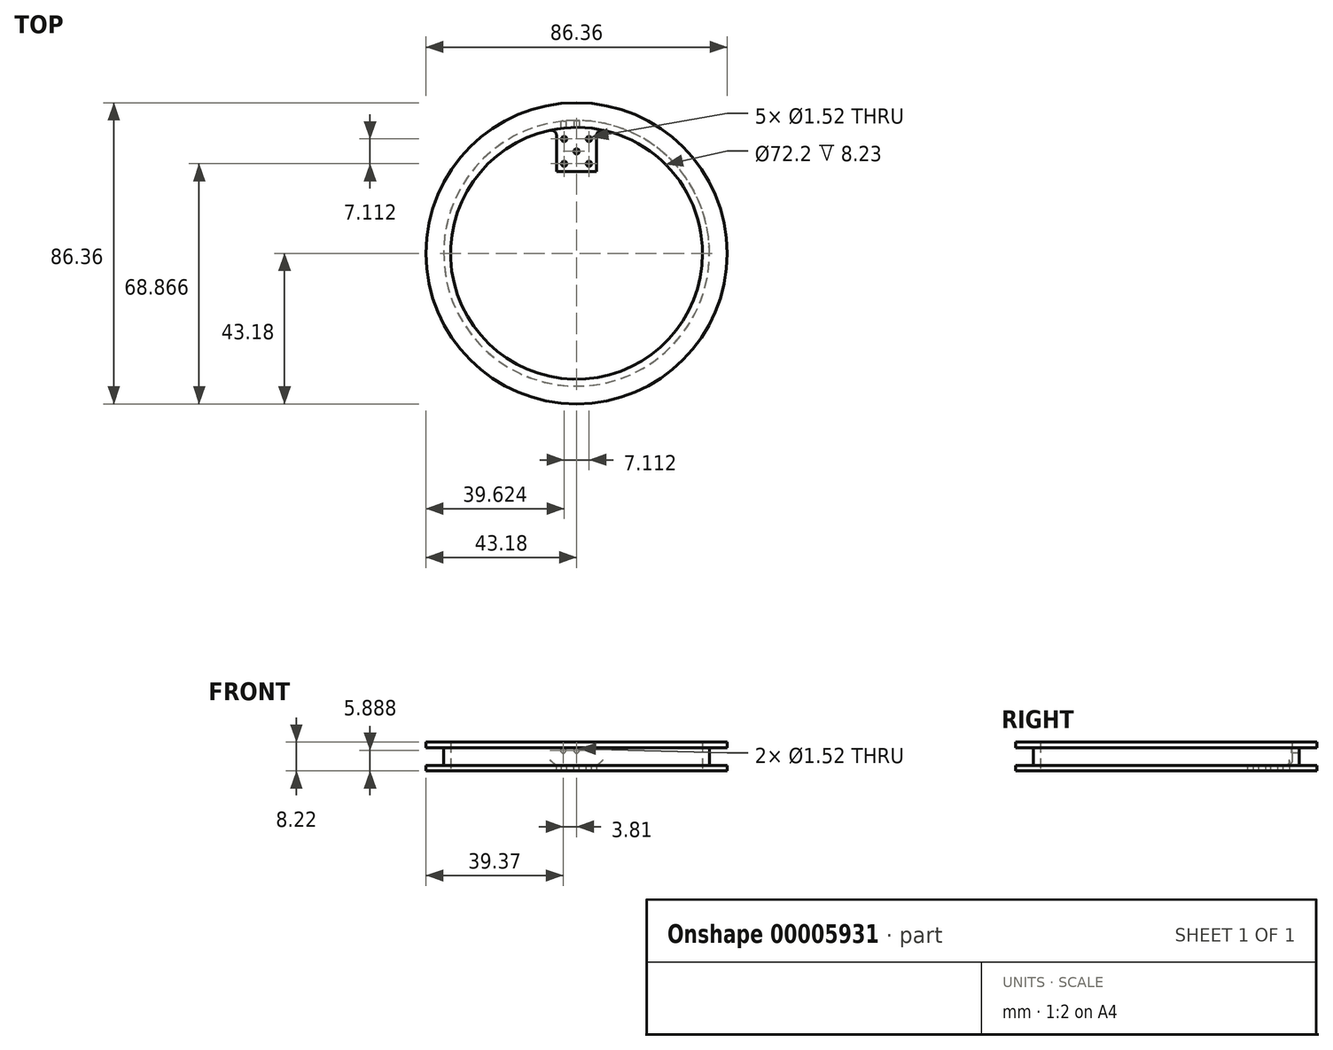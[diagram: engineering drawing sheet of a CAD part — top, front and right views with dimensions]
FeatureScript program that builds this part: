
annotation { "Feature Type Name" : "Feature", "Feature Type Description" : "" }
export const myFeature = defineFeature(function(context is Context, id is Id, definition is map)
    precondition{}
    {
        {
            var Q0;
            Q0=qCreatedBy(makeId("Top.planeOp"),FACE);
            var sketch = newSketch(context, id + "F0", { "sketchPlane" : qUnion([Q0])});
            skCircle(sketch, "E0", {"center": v(0, 0) * mm, "radius": 38.1 * mm});
            skCircle(sketch, "E1.0", {"center": v(0, 0) * mm, "radius": 36.1 * mm});
            skSolve(sketch);
        }
        {
            var Q0;
            Q0 = qSketchRegion(id + "F0", true);
            extrude(context, id + "F1", {"entities" : qUnion([Q0]), "depth" : 5.08 * mm});
        }
        {
            var Q0;
            Q0=qCreatedBy(makeId("Top.planeOp"),FACE);
            var sketch = newSketch(context, id + "F2", { "sketchPlane" : qUnion([Q0])});
            skCircle(sketch, "E2", {"center": v(0, 0) * mm, "radius": 43.18 * mm});
            skCircle(sketch, "E3", {"center": v(0, 0) * mm, "radius": 36.1 * mm});
            skSolve(sketch);
        }
        {
            var Q0;
            Q0 = qSketchRegion(id + "F2", true);
            extrude(context, id + "F3", {"entities" : qUnion([Q0]), "operationType" : NewBodyOperationType.ADD, "oppositeDirection" : true, "depth" : 1.57 * mm});
        }
        {
            var Q0;
            Q0=qCreatedBy(makeId("Top.planeOp"),FACE);
            var Q1;
            Q1=makeQuery(id+"F1.opExtrude","CAP_FACE",FACE,{"disambiguationData":[OSD([sQuery(id+"F0.wireOp",EDGE,"E0"),sQuery(id+"F0.wireOp",EDGE,"E1.0")])],"isStart":false});
            cPlane(context, id + "F4", {"entities" : qUnion([Q0, Q1]), "cplaneType" : CPlaneType.MID_PLANE, "offset" : 152.4 * mm, "width" : 152.4 * mm, "height" : 152.4 * mm});
        }
        {
            var Q0;
            Q0=makeQuery(id+"F1.opExtrude","SWEPT_BODY",BODY,{"disambiguationData":[OSD([sQuery(id+"F0.wireOp",EDGE,"E0"),sQuery(id+"F0.wireOp",EDGE,"E1.0")])]});
            var Q1;
            Q1=qCreatedBy(id+"F4.planeOp",FACE);
            mirror(context, id + "F5", {"entities" : qUnion([Q0]), "mirrorPlane" : qUnion([Q1])});
        }
        {
            var Q0;
            Q0=qCreatedBy(makeId("Top.planeOp"),FACE);
            var sketch = newSketch(context, id + "F6", { "sketchPlane" : qUnion([Q0])});
            skLineSegment(sketch, "E4.bottom", {"start": v(-5.72, 36.1) * mm, "end": v(5.72, 36.1) * mm});
            skLineSegment(sketch, "E4.top", {"start": v(-5.71, 23.4) * mm, "end": v(5.71, 23.4) * mm});
            skLineSegment(sketch, "E4.left", {"start": v(-5.72, 36.1) * mm, "end": v(-5.72, 23.4) * mm});
            skLineSegment(sketch, "E4.right", {"start": v(5.72, 36.1) * mm, "end": v(5.72, 23.4) * mm});
            skPoint(sketch, "E5", {"position": v(0, 36.1) * mm});
            skLineSegment(sketch, "E6.bottom", {"start": v(-3.56, 32.8) * mm, "end": v(3.56, 32.8) * mm, "construction": true});
            skLineSegment(sketch, "E6.top", {"start": v(-3.56, 25.69) * mm, "end": v(3.56, 25.69) * mm, "construction": true});
            skLineSegment(sketch, "E6.left", {"start": v(-3.56, 32.8) * mm, "end": v(-3.56, 25.69) * mm, "construction": true});
            skLineSegment(sketch, "E6.right", {"start": v(3.56, 32.8) * mm, "end": v(3.56, 25.69) * mm, "construction": true});
            skCircle(sketch, "E7", {"center": v(-3.56, 32.8) * mm, "radius": 0.76 * mm});
            skCircle(sketch, "E8", {"center": v(3.56, 32.8) * mm, "radius": 0.76 * mm});
            skCircle(sketch, "E9", {"center": v(3.56, 25.69) * mm, "radius": 0.76 * mm});
            skCircle(sketch, "E10", {"center": v(-3.56, 25.69) * mm, "radius": 0.76 * mm});
            skLineSegment(sketch, "E11", {"start": v(-3.56, 25.69) * mm, "end": v(3.56, 32.8) * mm, "construction": true});
            skCircle(sketch, "E12", {"center": v(0, 29.24) * mm, "radius": 0.76 * mm});
            skSolve(sketch);
        }
        {
            var Q0;
            Q0 = qSketchRegion(id + "F6", true);
            var Q1;
            Q1=makeQuery(id+"F3.opExtrude","CAP_FACE",FACE,{"disambiguationData":[OSD([sQuery(id+"F2.wireOp",EDGE,"E2"),sQuery(id+"F2.wireOp",EDGE,"E3")])],"isStart":false});
            extrude(context, id + "F7", {"entities" : qUnion([Q0]), "operationType" : NewBodyOperationType.ADD, "endBound" : BoundingType.UP_TO_SURFACE, "oppositeDirection" : true, "endBoundEntityFace" : qUnion([Q1]), "depth" : 25.4 * mm});
        }
        {
            var Q0;
            Q0=makeQuery(id+"F7.boolean.opBoolean","INTERSECT",EDGE,{"derivedFrom":[makeQuery(id+"F5.opPattern","COPY",FACE,{"derivedFrom":makeQuery(id+"F3.boolean.opBoolean","MERGE",FACE,{"derivedFrom":[makeQuery(id+"F1.opExtrude","SWEPT_FACE",FACE,{"disambiguationData":[OSD([sQuery(id+"F0.wireOp",EDGE,"E1.0")])]}),makeQuery(id+"F3.opExtrude","SWEPT_FACE",FACE,{"disambiguationData":[OSD([sQuery(id+"F2.wireOp",EDGE,"E3")])]})]}),"instanceName":"1"}),makeQuery(id+"F7.opExtrude","CAP_FACE",FACE,{"disambiguationData":[OSD([sQuery(id+"F6.wireOp",EDGE,"E4.bottom"),sQuery(id+"F6.wireOp",EDGE,"E4.top"),sQuery(id+"F6.wireOp",EDGE,"E4.left"),sQuery(id+"F6.wireOp",EDGE,"E4.right"),sQuery(id+"F6.wireOp",EDGE,"E7"),sQuery(id+"F6.wireOp",EDGE,"E8"),sQuery(id+"F6.wireOp",EDGE,"E9"),sQuery(id+"F6.wireOp",EDGE,"E10"),sQuery(id+"F6.wireOp",EDGE,"E12")])],"isStart":true})]});
            var Q1;
            Q1=makeQuery(id+"F7.boolean.opBoolean","INTERSECT",EDGE,{"derivedFrom":[makeQuery(id+"F5.opPattern","COPY",FACE,{"derivedFrom":makeQuery(id+"F3.boolean.opBoolean","MERGE",FACE,{"derivedFrom":[makeQuery(id+"F1.opExtrude","SWEPT_FACE",FACE,{"disambiguationData":[OSD([sQuery(id+"F0.wireOp",EDGE,"E1.0")])]}),makeQuery(id+"F3.opExtrude","SWEPT_FACE",FACE,{"disambiguationData":[OSD([sQuery(id+"F2.wireOp",EDGE,"E3")])]})]}),"instanceName":"1"}),makeQuery(id+"F7.opExtrude","SWEPT_FACE",FACE,{"disambiguationData":[OSD([sQuery(id+"F6.wireOp",EDGE,"E4.right")])]})]});
            var Q2;
            Q2=makeQuery(id+"F7.boolean.opBoolean","INTERSECT",EDGE,{"derivedFrom":[makeQuery(id+"F5.opPattern","COPY",FACE,{"derivedFrom":makeQuery(id+"F3.boolean.opBoolean","MERGE",FACE,{"derivedFrom":[makeQuery(id+"F1.opExtrude","SWEPT_FACE",FACE,{"disambiguationData":[OSD([sQuery(id+"F0.wireOp",EDGE,"E1.0")])]}),makeQuery(id+"F3.opExtrude","SWEPT_FACE",FACE,{"disambiguationData":[OSD([sQuery(id+"F2.wireOp",EDGE,"E3")])]})]}),"instanceName":"1"}),makeQuery(id+"F7.opExtrude","SWEPT_FACE",FACE,{"disambiguationData":[OSD([sQuery(id+"F6.wireOp",EDGE,"E4.left")])]})]});
            fillet(context, id + "F8", {"entities" : qUnion([Q0, Q1, Q2]), "radius" : 1.57 * mm, "tangentPropagation" : true, "allowEdgeOverflow" : false});
        }
        {
            var Q0;
            Q0=qCreatedBy(makeId("Front.planeOp"),FACE);
            var sketch = newSketch(context, id + "F9", { "sketchPlane" : qUnion([Q0])});
            skCircle(sketch, "E13", {"center": v(0, 4.32) * mm, "radius": 0.76 * mm});
            skLineSegment(sketch, "E14", {"start": v(0, 4.32) * mm, "end": v(-3.81, 4.32) * mm, "construction": true});
            skCircle(sketch, "E15", {"center": v(-3.81, 4.32) * mm, "radius": 0.76 * mm});
            skSolve(sketch);
        }
        {
            var Q0;
            Q0 = qSketchRegion(id + "F9", true);
            extrude(context, id + "F10", {"entities" : qUnion([Q0]), "operationType" : NewBodyOperationType.REMOVE, "endBound" : BoundingType.THROUGH_ALL, "oppositeDirection" : true, "depth" : 25.4 * mm});
        }
    });
